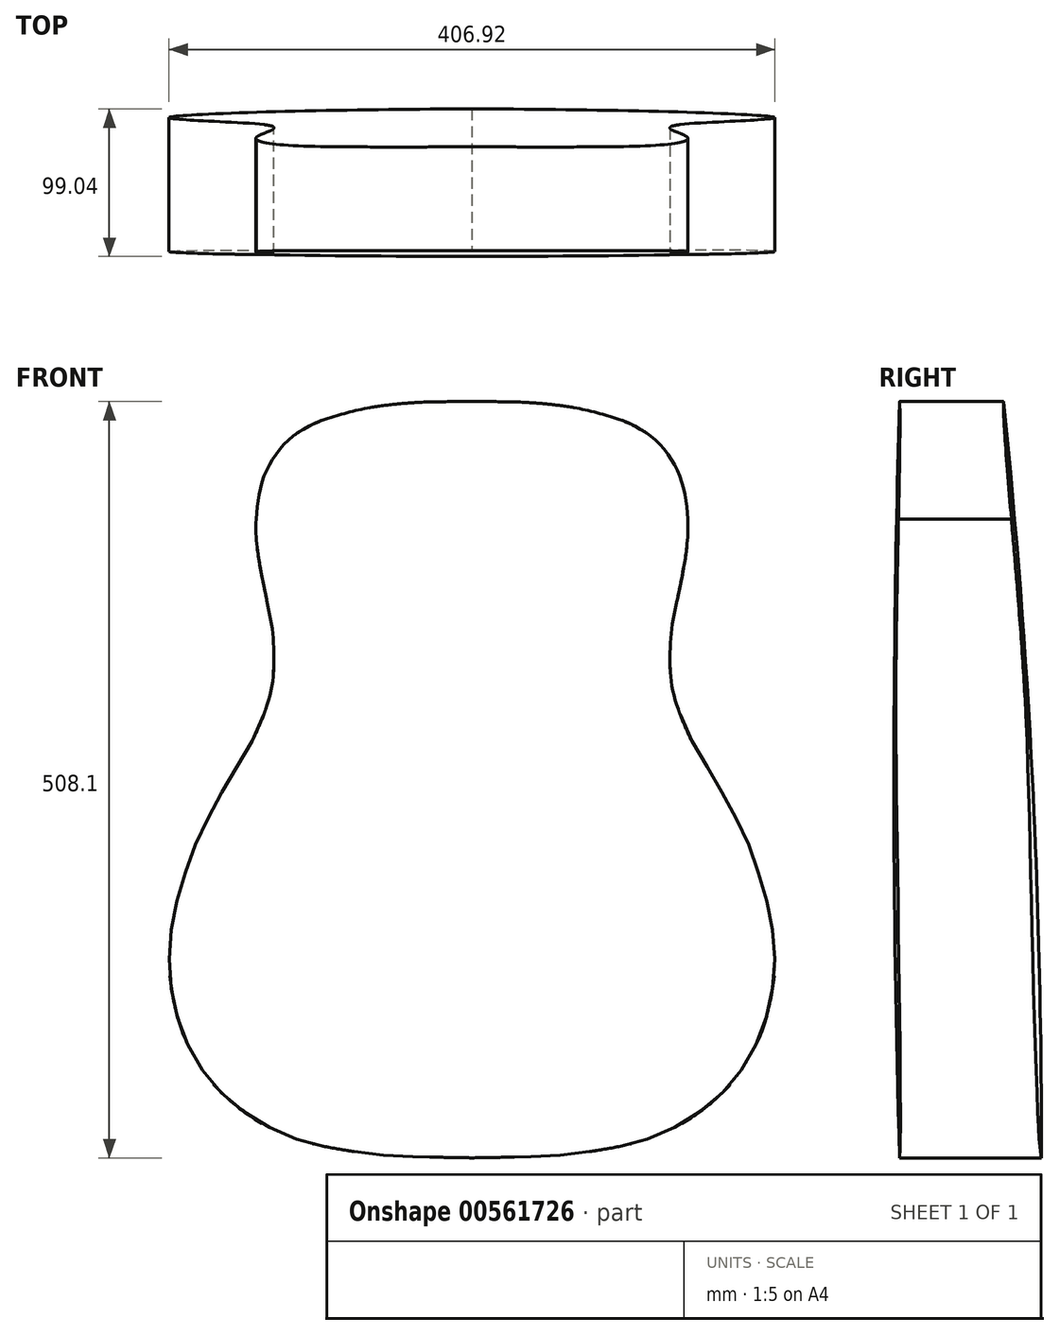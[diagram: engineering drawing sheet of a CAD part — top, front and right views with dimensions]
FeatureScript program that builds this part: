
annotation { "Feature Type Name" : "Feature", "Feature Type Description" : "" }
export const myFeature = defineFeature(function(context is Context, id is Id, definition is map)
    precondition{}
    {
        {
            var Q0;
            Q0=qCreatedBy(makeId("Front.planeOp"),FACE);
            var sketch = newSketch(context, id + "F0", { "sketchPlane" : qUnion([Q0])});
            skLineSegment(sketch, "E0", {"start": v(0, 213.41) * mm, "end": v(-60.32, 213.41) * mm});
            skArc(sketch, "E1", {"start": v(-60.32, 213.41) * mm, "mid": v(-123.9, 185.19) * mm, "end": v(-145.62, 119.1) * mm});
            skLineSegment(sketch, "E2", {"start": v(-44.45, -294.59) * mm, "end": v(0, -294.59) * mm});
            skArc(sketch, "E3", {"start": v(-44.45, -294.59) * mm, "mid": v(-83.6, -290.39) * mm, "end": v(-120.97, -277.97) * mm});
            skArc(sketch, "E4", {"start": v(-120.97, -277.97) * mm, "mid": v(-199.06, -184) * mm, "end": v(-174.01, -64.4) * mm});
            skLineSegment(sketch, "E5", {"start": v(-174.01, -64.4) * mm, "end": v(-165, -52.7) * mm});
            skArc(sketch, "E6", {"start": v(-165, -52.7) * mm, "mid": v(-138.92, 1.9) * mm, "end": v(-137.44, 62.4) * mm});
            skArc(sketch, "E7", {"start": v(-137.44, 62.4) * mm, "mid": v(-142.14, 90.66) * mm, "end": v(-145.62, 119.1) * mm});
            skArc(sketch, "E8.MirrorCS", {"start": v(44.45, -294.59) * mm, "mid": v(83.6, -290.39) * mm, "end": v(120.97, -277.97) * mm});
            skLineSegment(sketch, "E9.MirrorCS", {"start": v(174.01, -64.4) * mm, "end": v(165, -52.7) * mm});
            skArc(sketch, "E10.MirrorCS", {"start": v(165, -52.7) * mm, "mid": v(138.92, 1.9) * mm, "end": v(137.44, 62.4) * mm});
            skArc(sketch, "E11.MirrorCS", {"start": v(120.97, -277.97) * mm, "mid": v(199.06, -184) * mm, "end": v(174.01, -64.4) * mm});
            skArc(sketch, "E12.MirrorCS", {"start": v(137.44, 62.4) * mm, "mid": v(142.14, 90.66) * mm, "end": v(145.62, 119.1) * mm});
            skLineSegment(sketch, "E13.MirrorCS", {"start": v(0, 213.41) * mm, "end": v(60.32, 213.41) * mm});
            skLineSegment(sketch, "E14.MirrorCS", {"start": v(44.45, -294.59) * mm, "end": v(0, -294.59) * mm});
            skArc(sketch, "E15.MirrorCS", {"start": v(60.32, 213.41) * mm, "mid": v(123.9, 185.19) * mm, "end": v(145.62, 119.1) * mm});
            skLineSegment(sketch, "E16", {"start": v(-146.05, 127.69) * mm, "end": v(146.05, 127.69) * mm, "construction": true});
            skLineSegment(sketch, "E17", {"start": v(-134.94, 35.61) * mm, "end": v(134.94, 35.61) * mm, "construction": true});
            skLineSegment(sketch, "E18", {"start": v(-203.2, -150.12) * mm, "end": v(203.2, -150.12) * mm, "construction": true});
            skLineSegment(sketch, "E19", {"start": v(0, 213.41) * mm, "end": v(0, -358.14) * mm});
            skFitSpline(sketch, "E20", {"points": [v(0, -358.14) * mm, v(-31.15, -357.54) * mm, v(-59.16, -356.62) * mm, v(-86.9, -353.64) * mm, v(-118.48, -347.89) * mm, v(-143.81, -339.6) * mm, v(-161.64, -330.25) * mm, v(-180.06, -317.2) * mm, v(-194.24, -303.7) * mm, v(-204.72, -290.2) * mm, v(-216.69, -268.12) * mm, v(-223.01, -249.42) * mm, v(-227.61, -226.68) * mm, v(-228.82, -205.73) * mm, v(-226.86, -183.23) * mm, v(-223.36, -165.75) * mm, v(-216.08, -141.3) * mm, v(-211.1, -126.4) * mm, v(-206.26, -114.7) * mm, v(-199.18, -100.73) * mm, v(-187.54, -79.5) * mm, v(-174.73, -57.5) * mm, v(-169.53, -49.05) * mm, v(-164.5, -39.87) * mm, v(-161.42, -32.99) * mm, v(-158.26, -25.51) * mm, v(-156.15, -19.96) * mm, v(-154.21, -13.95) * mm, v(-152.46, -7.92) * mm, v(-150.6, 1.32) * mm, v(-150.05, 7.66) * mm, v(-149.67, 13.77) * mm, v(-149.67, 19.91) * mm, v(-149.66, 24.94) * mm, v(-150, 31.24) * mm, v(-150.43, 37.59) * mm, v(-151.5, 45.78) * mm, v(-155.2, 63.95) * mm, v(-158.64, 80.97) * mm, v(-161.74, 98.9) * mm, v(-163.26, 117.74) * mm, v(-162.16, 131.87) * mm, v(-158.5, 145.23) * mm, v(-153.65, 154.96) * mm, v(-145.76, 166.4) * mm, v(-137.96, 175.03) * mm, v(-128.22, 184.46) * mm, v(-118.3, 191.75) * mm, v(-105.15, 199.26) * mm, v(-90.14, 204.94) * mm, v(-76.37, 208.48) * mm, v(-58.55, 211.27) * mm, v(-41.73, 212.73) * mm, v(0, 213.41) * mm], "startDerivative": vector(-1172.44, 22.67) * mm, "endDerivative": vector(2148.85, 0) * mm});
            skFitSpline(sketch, "E21", {"points": [v(-155.2, 63.95) * mm, v(-152.28, 40.95) * mm, v(-151.19, 24.94) * mm, v(-151.56, 7.64) * mm, v(-157.24, -22.95) * mm], "startDerivative": vector(19.77, -92.42) * mm, "endDerivative": vector(-43.1, -109.65) * mm});
            skFitSpline(sketch, "E22", {"points": [v(-163.08, 124.46) * mm, v(-158.69, 152.26) * mm, v(-155.07, 161.86) * mm, v(-147.82, 173.9) * mm, v(-140.73, 182.43) * mm, v(-131.36, 189.95) * mm, v(-118.18, 197.2) * mm, v(-106.49, 201.54) * mm, v(-85.07, 207.2) * mm, v(-41.73, 212.73) * mm], "startDerivative": vector(18.61, 314.15) * mm, "endDerivative": vector(340.78, 21.24) * mm});
            skSolve(sketch);
        }
        {
            var Q0;
            {var subQ0=sQuery(id+"F0.wireOp",EDGE,"E3");Q0=makeQuery(id+"F0.imprint","IMPRINT",FACE,{"disambiguationData":[TD([[makeQuery(id+"F0.imprint","IMPRINT",EDGE,{"derivedFrom":subQ0}),-1.0]])]});}
            var Q1;
            {var subQ0=sQuery(id+"F0.wireOp",EDGE,"E3");Q1=makeQuery(id+"F0.imprint","IMPRINT",FACE,{"disambiguationData":[TD([[makeQuery(id+"F0.imprint","IMPRINT",EDGE,{"derivedFrom":subQ0}),1.0]])]});}
            var Q2;
            {var subQ0=sQuery(id+"F0.wireOp",EDGE,"E21");var subQ1=sQuery(id+"F0.wireOp",EDGE,"E20");var subQ2=makeQuery(id+"F0.imprint","INTERSECT",VERTEX,{"disambiguationData":[OD(3.0)],"derivedFrom":[subQ1,subQ0]});Q2=makeQuery(id+"F0.imprint","IMPRINT",FACE,{"disambiguationData":[TD([[makeQuery(id+"F0.imprint","IMPRINT",EDGE,{"disambiguationData":[TD([[subQ2,-1.0]])],"derivedFrom":subQ1}),1.0]])]});}
            var Q3;
            {var subQ0=sQuery(id+"F0.wireOp",EDGE,"E22");var subQ1=sQuery(id+"F0.wireOp",EDGE,"E1");var subQ2=makeQuery(id+"F0.imprint","INTERSECT",VERTEX,{"derivedFrom":[subQ1,subQ0]});Q3=makeQuery(id+"F0.imprint","IMPRINT",FACE,{"disambiguationData":[TD([[makeQuery(id+"F0.imprint","IMPRINT",EDGE,{"disambiguationData":[TD([[subQ2,-1.0]])],"derivedFrom":subQ1}),-1.0]])]});}
            var Q4;
            {var subQ0=sQuery(id+"F0.wireOp",EDGE,"E22");var subQ1=sQuery(id+"F0.wireOp",EDGE,"E1");var subQ2=makeQuery(id+"F0.imprint","INTERSECT",VERTEX,{"derivedFrom":[subQ1,subQ0]});Q4=makeQuery(id+"F0.imprint","IMPRINT",FACE,{"disambiguationData":[TD([[makeQuery(id+"F0.imprint","IMPRINT",EDGE,{"disambiguationData":[TD([[subQ2,-1.0]])],"derivedFrom":subQ1}),1.0]])]});}
            var Q5;
            {var subQ0=sQuery(id+"F0.wireOp",EDGE,"88b0a920-b310-4c35-a5f5-957b590fef5f");var subQ1=sQuery(id+"F0.wireOp",EDGE,"E20");var subQ2=makeQuery(id+"F0.imprint","INTERSECT",VERTEX,{"disambiguationData":[OD(3.0)],"derivedFrom":[subQ1,subQ0]});Q5=makeQuery(id+"F0.imprint","IMPRINT",FACE,{"disambiguationData":[TD([[makeQuery(id+"F0.imprint","IMPRINT",EDGE,{"disambiguationData":[TD([[subQ2,-1.0]])],"derivedFrom":subQ1}),-1.0]])]});}
            extrude(context, id + "F1", {"entities" : qUnion([Q0, Q1, Q2, Q3, Q4, Q5]), "endBound" : BoundingType.SYMMETRIC, "depth" : 254 * mm, "offsetDistance" : 25.4 * mm});
        }
        {
            var Q0;
            Q0=makeQuery(id+"F1.opExtrude","SWEPT_BODY",BODY,{"disambiguationData":[OSD([sQuery(id+"F0.wireOp",EDGE,"E19"),sQuery(id+"F0.wireOp",EDGE,"E20")])]});
            var Q1;
            Q1=sQuery(id+"F0.wireOp",VERTEX,"E20.53.internal");
            transform(context, id + "F2", {"entities" : qUnion([Q0]), "transformType" : TransformType.SCALE_UNIFORMLY, "scale" : .889, "scalePoint" : qUnion([Q1]), "makeCopy" : false});
        }
        {
            var Q0;
            Q0=qCreatedBy(makeId("Right.planeOp"),FACE);
            var sketch = newSketch(context, id + "F3", { "sketchPlane" : qUnion([Q0])});
            skLineSegment(sketch, "E23", {"start": v(0, -294.7) * mm, "end": v(-25.4, 213.41) * mm, "construction": true});
            skArc(sketch, "E24", {"start": v(0, -294.7) * mm, "mid": v(-6.07, -40.3) * mm, "end": v(-25.4, 213.41) * mm, "construction": true});
            skArc(sketch, "E25", {"start": v(-95.25, 213.41) * mm, "mid": v(-99.03, -40.64) * mm, "end": v(-95.25, -294.7) * mm, "construction": true});
            skLineSegment(sketch, "E26", {"start": v(-25.4, 213.41) * mm, "end": v(-95.25, 213.41) * mm});
            skLineSegment(sketch, "E27", {"start": v(0, -294.7) * mm, "end": v(-95.25, -294.7) * mm});
            skLineSegment(sketch, "E28", {"start": v(-95.25, 213.41) * mm, "end": v(-95.25, -294.7) * mm, "construction": true});
            skLineSegment(sketch, "E29", {"start": v(-12.7, -40.64) * mm, "end": v(-35.24, -41.77) * mm, "construction": true});
            skLineSegment(sketch, "E30", {"start": v(-95.25, -40.64) * mm, "end": v(-73.58, -40.64) * mm, "construction": true});
            skArc(sketch, "E31", {"start": v(-48.38, -969.1) * mm, "mid": v(-0.8, -194.73) * mm, "end": v(-76.63, 577.38) * mm});
            skArc(sketch, "E32", {"start": v(-76.63, 577.38) * mm, "mid": v(-97.6, -196.5) * mm, "end": v(-48.38, -969.1) * mm});
            skLineSegment(sketch, "E33.bottom", {"start": v(304.69, 337.75) * mm, "end": v(-324.28, 337.75) * mm});
            skLineSegment(sketch, "E33.top", {"start": v(304.69, -421.05) * mm, "end": v(-324.28, -421.05) * mm});
            skLineSegment(sketch, "E33.left", {"start": v(304.69, 337.75) * mm, "end": v(304.69, -421.05) * mm});
            skLineSegment(sketch, "E33.right", {"start": v(-324.28, 337.75) * mm, "end": v(-324.28, -421.05) * mm});
            skLineSegment(sketch, "E34", {"start": v(-12.7, -40.64) * mm, "end": v(304.69, -24.77) * mm});
            skLineSegment(sketch, "E35", {"start": v(-95.25, -40.64) * mm, "end": v(-324.28, -40.64) * mm});
            skSolve(sketch);
        }
        {
            var Q0;
            {var subQ3=sQuery(id+"F3.wireOp",EDGE,"E31");var subQ5=makeQuery(id+"F3.imprint","INTERSECT",VERTEX,{"derivedFrom":[sQuery(id+"F3.wireOp",EDGE,"E26"),subQ3]});Q0=makeQuery(id+"F3.imprint","IMPRINT",FACE,{"disambiguationData":[TD([[makeQuery(id+"F3.imprint","IMPRINT",EDGE,{"disambiguationData":[TD([[subQ5,1.0]])],"derivedFrom":subQ3}),-1.0]])]});}
            var Q1;
            Q1=sQuery(id+"F3.wireOp",EDGE,"E34");
            revolve(context, id + "F4", {"operationType" : NewBodyOperationType.REMOVE, "entities" : qUnion([Q0]), "axis" : qUnion([Q1]), "revolveType" : RevolveType.FULL, "oppositeDirection" : true});
        }
        {
            var Q0;
            {var subQ5=sQuery(id+"F3.wireOp",EDGE,"E32");var subQ7=makeQuery(id+"F3.imprint","INTERSECT",VERTEX,{"derivedFrom":[sQuery(id+"F3.wireOp",EDGE,"E26"),subQ5]});Q0=makeQuery(id+"F3.imprint","IMPRINT",FACE,{"disambiguationData":[TD([[makeQuery(id+"F3.imprint","IMPRINT",EDGE,{"disambiguationData":[TD([[subQ7,1.0]])],"derivedFrom":subQ5}),-1.0]])]});}
            var Q1;
            Q1=sQuery(id+"F3.wireOp",EDGE,"E35");
            revolve(context, id + "F5", {"operationType" : NewBodyOperationType.REMOVE, "entities" : qUnion([Q0]), "axis" : qUnion([Q1]), "revolveType" : RevolveType.FULL, "oppositeDirection" : true});
        }
        {
            var Q0;
            Q0=makeQuery(id+"F1.opExtrude","SWEPT_BODY",BODY,{"disambiguationData":[OSD([sQuery(id+"F0.wireOp",EDGE,"E19"),sQuery(id+"F0.wireOp",EDGE,"E20")])]});
            var Q1;
            {var subQ3=sQuery(id+"F3.wireOp",EDGE,"E26");Q1=makeQuery(id+"F3.imprint","IMPRINT",FACE,{"disambiguationData":[TD([[makeQuery(id+"F3.imprint","IMPRINT",EDGE,{"derivedFrom":subQ3}),1.0]])]});}
            mirror(context, id + "F6", {"operationType" : NewBodyOperationType.ADD, "entities" : qUnion([Q0]), "mirrorPlane" : qUnion([Q1])});
        }
    });
